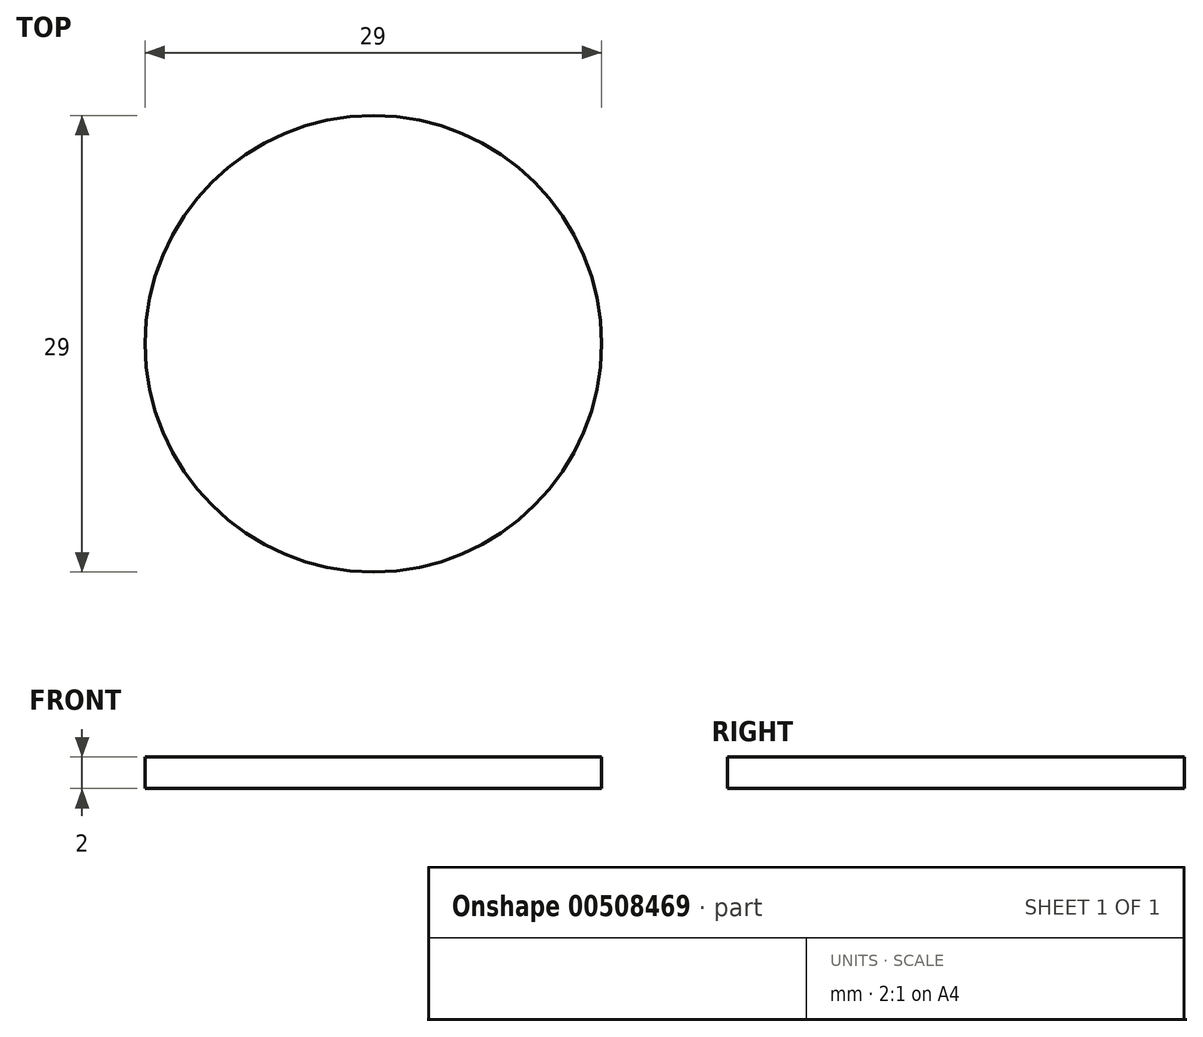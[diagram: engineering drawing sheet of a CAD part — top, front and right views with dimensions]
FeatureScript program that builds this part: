
annotation { "Feature Type Name" : "Feature", "Feature Type Description" : "" }
export const myFeature = defineFeature(function(context is Context, id is Id, definition is map)
    precondition{}
    {
        {
            var Q0;
            Q0=qCreatedBy(makeId("Top.planeOp"),FACE);
            var sketch = newSketch(context, id + "F0", { "sketchPlane" : qUnion([Q0])});
            skCircle(sketch, "E0", {"center": v(0, 0) * mm, "radius": 14.5 * mm});
            skSolve(sketch);
        }
        {
            var Q0;
            Q0=makeQuery(id+"F0.imprint","IMPRINT",FACE,{"disambiguationData":[TD([[makeQuery(id+"F0.imprint","IMPRINT",EDGE,{"derivedFrom":sQuery(id+"F0.wireOp",EDGE,"E0")}),1.0]])]});
            extrude(context, id + "F1", {"entities" : qUnion([Q0]), "depth" : 2 * mm});
        }
    });
